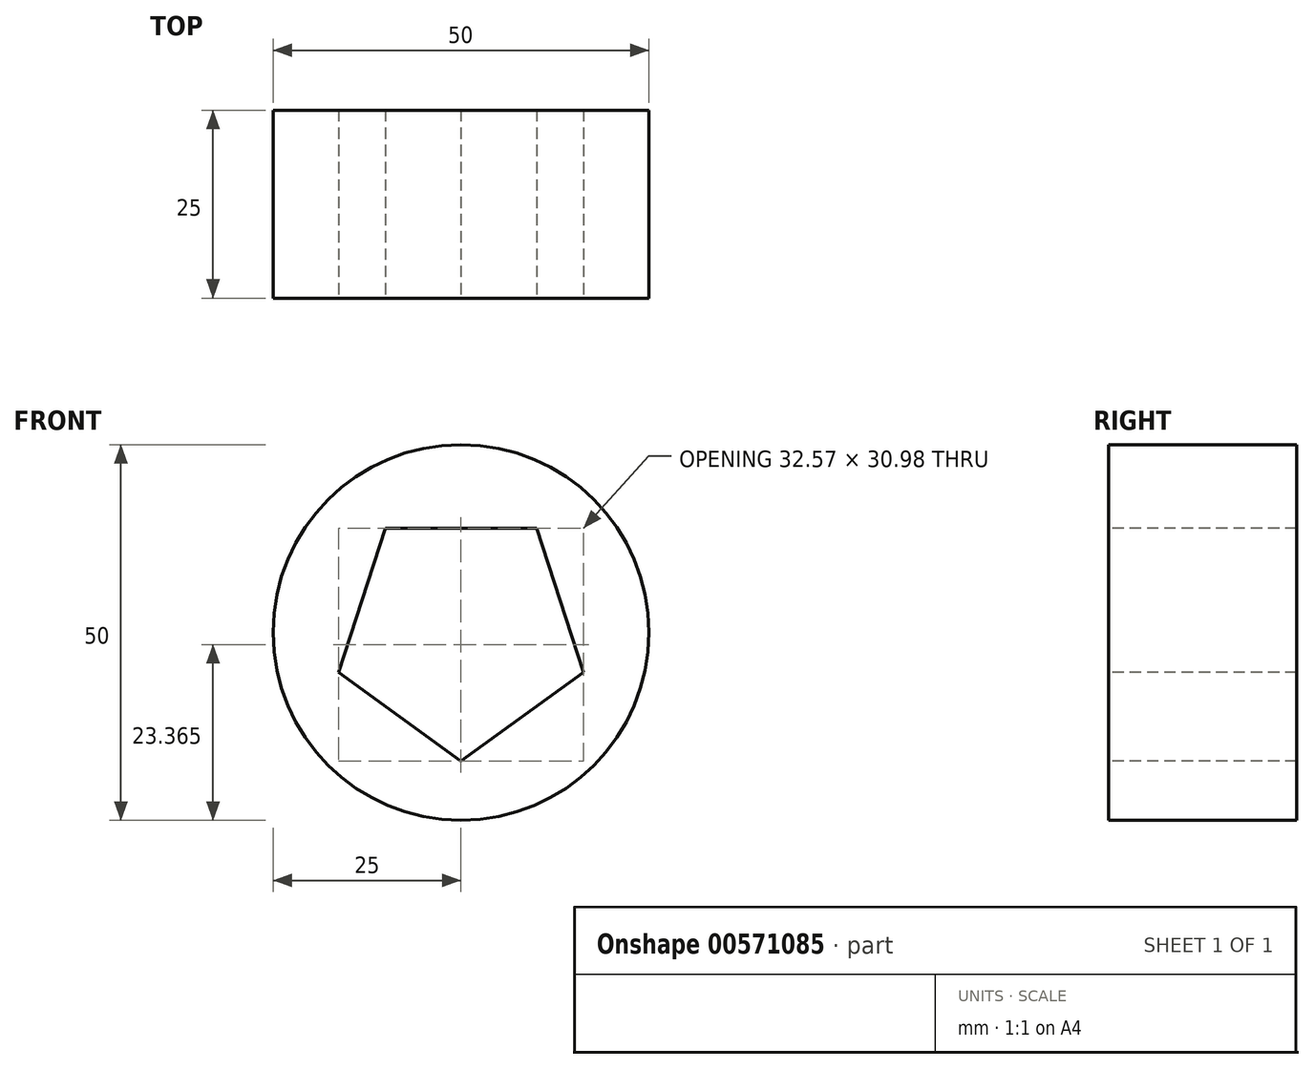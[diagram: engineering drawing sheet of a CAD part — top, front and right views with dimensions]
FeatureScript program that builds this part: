
annotation { "Feature Type Name" : "Feature", "Feature Type Description" : "" }
export const myFeature = defineFeature(function(context is Context, id is Id, definition is map)
    precondition{}
    {
        {
            var Q0;
            Q0=qCreatedBy(makeId("Front.planeOp"),FACE);
            var sketch = newSketch(context, id + "F0", { "sketchPlane" : qUnion([Q0])});
            skCircle(sketch, "E0", {"center": v(0, 0) * mm, "radius": 25 * mm});
            skSolve(sketch);
        }
        {
            var Q0;
            Q0=makeQuery(id+"F0.imprint","IMPRINT",FACE,{"disambiguationData":[TD([[makeQuery(id+"F0.imprint","IMPRINT",EDGE,{"derivedFrom":sQuery(id+"F0.wireOp",EDGE,"E0")}),1.0]])]});
            extrude(context, id + "F1", {"entities" : qUnion([Q0]), "depth" : 25 * mm, "offsetDistance" : 25 * mm});
        }
        {
            var Q0;
            Q0=makeQuery(id+"F1.opExtrude","CAP_FACE",FACE,{"disambiguationData":[OSD([sQuery(id+"F0.wireOp",EDGE,"E0")])],"isStart":false});
            var sketch = newSketch(context, id + "F2", { "sketchPlane" : qUnion([Q0])});
            skCircle(sketch, "E1.cCircle", {"center": v(0, 0) * mm, "radius": 13.85 * mm, "construction": true});
            skLineSegment(sketch, "E1.0", {"start": v(10.07, 13.85) * mm, "end": v(16.29, -5.3) * mm});
            skLineSegment(sketch, "E1.1", {"start": v(16.29, -5.3) * mm, "end": v(0, -17.13) * mm});
            skLineSegment(sketch, "E1.2", {"start": v(0, -17.13) * mm, "end": v(-16.29, -5.3) * mm});
            skLineSegment(sketch, "E1.3", {"start": v(-16.29, -5.3) * mm, "end": v(-10.06, 13.86) * mm});
            skLineSegment(sketch, "E1.4", {"start": v(-10.06, 13.86) * mm, "end": v(10.07, 13.85) * mm});
            skPoint(sketch, "E1.0.midPoint", {"position": v(13.18, 4.28) * mm});
            skSolve(sketch);
        }
        {
            var Q0;
            Q0=makeQuery(id+"F2.imprint","IMPRINT",FACE,{"disambiguationData":[TD([[makeQuery(id+"F2.imprint","IMPRINT",EDGE,{"derivedFrom":sQuery(id+"F2.wireOp",EDGE,"E1.0")}),-1.0]])]});
            extrude(context, id + "F3", {"entities" : qUnion([Q0]), "operationType" : NewBodyOperationType.REMOVE, "oppositeDirection" : true, "depth" : 25 * mm, "offsetDistance" : 25 * mm});
        }
    });
